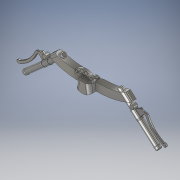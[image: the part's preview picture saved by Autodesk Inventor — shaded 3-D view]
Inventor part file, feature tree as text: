
AUTODESK INVENTOR PART (.ipt)
format: ipt  version: 2018 (Build 220112000, 112)  size: 634,880 bytes
history: native  units: in
note: dims shown in document units (in); Inventor stores cm internally (conversion verified against a paired STEP export)
features: extrude x17, fillet x15, sketch x10, plane x5, mirror x3, revolve x3
ambient origin geometry x8: Origin, YZ Plane, XZ Plane, XY Plane, X Axis, Y Axis, Z Axis, Center Point
bodies: Solid1 (feature_tree)
feature tree (53):
  sketch  "Sketch1"  dims[d2=1.4567in d3=2.2441in]
  extrude  "Extrusion1"  Depth=2.2441in
  extrude  "Extrusion2"  Depth=1.4567in
  extrude  "Extrusion3"  Depth=1.1811in TaperAngle=0.0deg
  extrude  "Extrusion4"  Depth=0.5906in TaperAngle=0.0deg
  fillet  "Fillet1"  Radius=0.5906in
  fillet  "Fillet2"  Radius=0.5906in
  fillet  "Fillet3"  Radius=0.5906in
  fillet  "Fillet4"  Radius=0.5906in
  fillet  "Fillet5"  Radius=0.5906in
  fillet  "Fillet6"  Radius=0.5906in
  sketch  "Sketch2"  dims[d6=0.7874in d9=1.4567in]
  plane  "Work Plane1"
  extrude  "Extrusion5"  Depth=0.5906in
  fillet  "Fillet7"  Radius=0.5906in
  fillet  "Fillet8"  Radius=0.1378in
  fillet  "Fillet9"  Radius=0.1181in
  mirror  "Mirror1"
  plane  "Work Plane3"
  sketch  "Sketch4"  dims[d13=2.3622in d14=0.0in d15=1.1811in d16=0.0in d17=0.5906in d18=0.0in d19=0.5906in d20=0.5906in d21=0.5906in d22=0.5906in d23=0.5906in]
  revolve  "Revolution1"  [1 undecoded]
  revolve  "Revolution2"  [1 undecoded]
  revolve  "Revolution3"  Angle=90.0deg
  extrude  "Extrusion6"  Depth=0.0394in
  fillet  "Fillet10"  [1 undecoded]
  mirror  "Mirror2"
  sketch  "Sketch5"  dims[d24=0.5906in d27=0.9449in]
  sketch  "Sketch6"  dims[d28=7.0866in d29=2.4902in d30=0.0in d31=0.0in d32=0.5906in d33=0.1378in d34=0.1181in]
  plane  "Work Plane5"
  sketch  "Sketch7"  dims[d35=-0.5906in d36=0.1181in]
  extrude  "Extrusion7"  Depth=0.9843in
  extrude  "Extrusion8"  Depth=0.9843in TaperAngle=0.0deg
  extrude  "Extrusion9"  Depth=0.9843in
  sketch  "Sketch8"  dims[d37=90.0deg d38=4.0551in]
  extrude  "Extrusion10"  Depth=0.9843in
  extrude  "Extrusion11"  Depth=0.9843in TaperAngle=0.0deg
  extrude  "Extrusion12"  Depth=0.9843in TaperAngle=0.0deg
  extrude  "Extrusion13"  Depth=0.9843in TaperAngle=0.0deg
  extrude  "Extrusion14"  Depth=0.0394in TaperAngle=0.0deg
  extrude  "Extrusion15"  Depth=0.0394in TaperAngle=0.0deg
  fillet  "Fillet11"  Radius=0.0787in
  fillet  "Fillet12"  Radius=0.0787in
  fillet  "Fillet13"  Radius=0.1181in
  extrude  "Extrusion16"  Depth=0.9843in TaperAngle=0.0deg
  fillet  "Fillet15"  Radius=0.0197in
  fillet  "Fillet16"  Radius=0.0197in
  mirror  "Mirror3"
  extrude  "Extrusion17"  Depth=0.9843in
  sketch  "Sketch3"  dims[d10=15.0574in d11=1.1811in d12=0.0in]
  plane  "Work Plane2"
  plane  "Work Plane4"
  sketch  "Sketch9"  dims[d39=0.1181in d40=90.0deg]
  sketch  "Sketch10"  dims[d41=1.378in d42=0.0394in d43=90.0deg d44=0.7874in d45=0.7874in d46=0.0in d47=0.0591in d48=1.1875in d52=0.1969in d53=0.0in d54=0.1969in d55=0.0in d56=0.0984in d57=0.315in d58=0.0in d59=0.0in d65=0.0394in d66=0.0in d67=0.0394in d68=0.0in d69=0.0787in d70=0.0in d71=0.0787in d72=0.0in d73=0.1181in d74=0.0in d75=0.1181in d76=0.0in d77=0.0197in d78=0.0197in d79=0.0197in d85=1.2598in d86=0.315in d87=0.0in d88=0.0394in d89=0.0394in d90=1.1811in d91=0.9843in d92=0.0in]
note: 3 required parameter values undecoded (feature->parameter linkage not recoverable at this tier; creation-order binding heuristic only, values carry confidence <= 0.55)